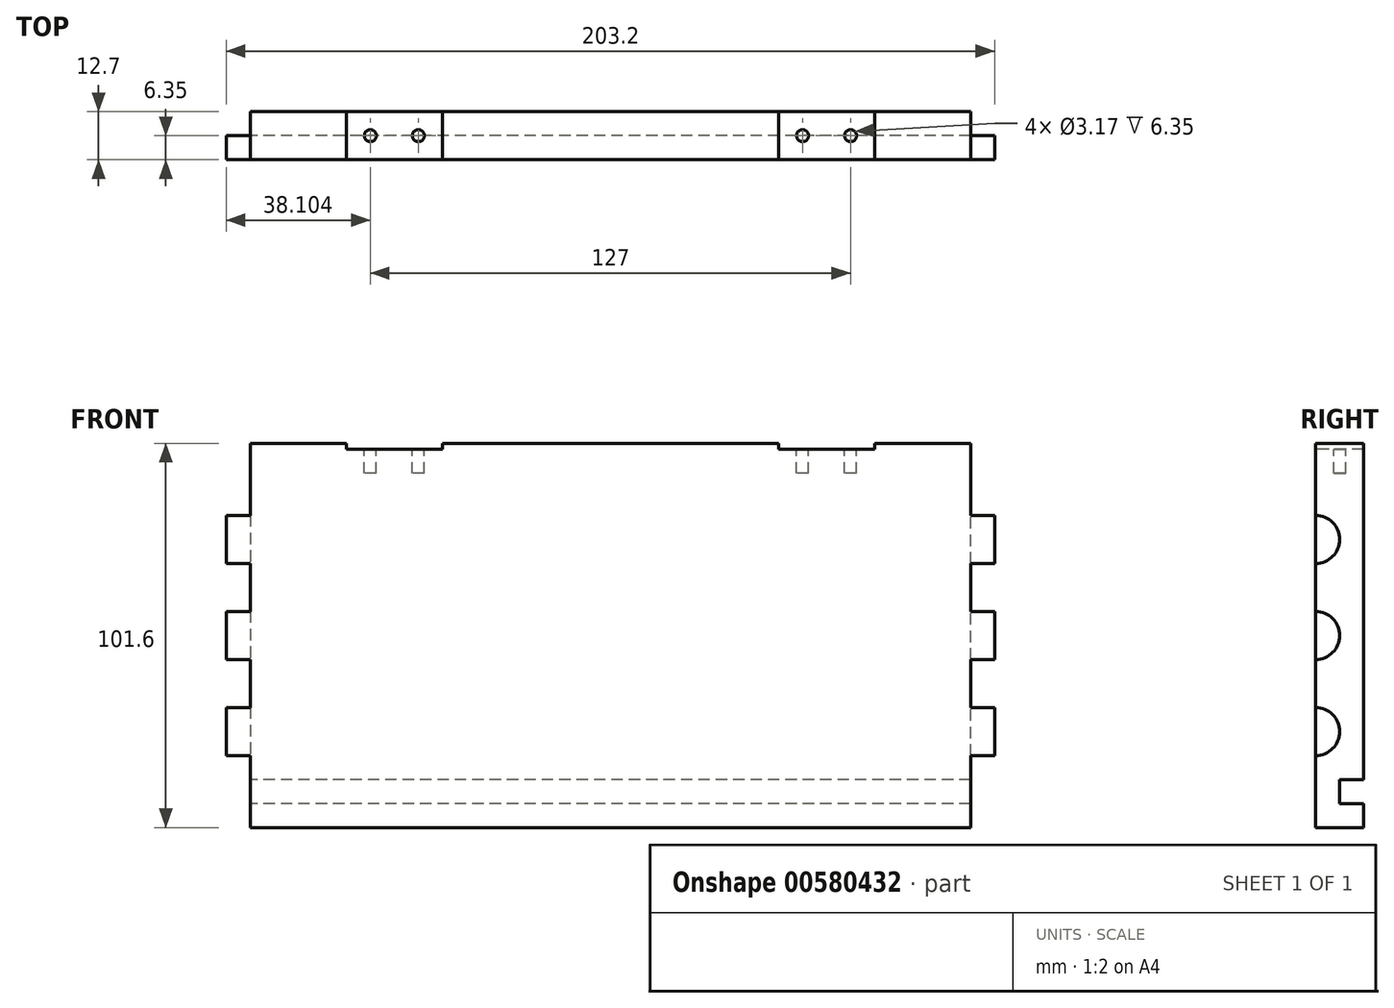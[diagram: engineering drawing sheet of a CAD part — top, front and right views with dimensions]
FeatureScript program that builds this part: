
annotation { "Feature Type Name" : "Feature", "Feature Type Description" : "" }
export const myFeature = defineFeature(function(context is Context, id is Id, definition is map)
    precondition{}
    {
        {
            var Q0;
            Q0=qCreatedBy(makeId("Front.planeOp"),FACE);
            var sketch = newSketch(context, id + "F0", { "sketchPlane" : qUnion([Q0])});
            skLineSegment(sketch, "E0.bottom", {"start": v(104.93, 50.8) * mm, "end": v(-98.27, 50.8) * mm});
            skLineSegment(sketch, "E0.top", {"start": v(104.93, -50.8) * mm, "end": v(-98.27, -50.8) * mm});
            skLineSegment(sketch, "E0.left", {"start": v(104.93, 50.8) * mm, "end": v(104.93, -50.8) * mm});
            skLineSegment(sketch, "E0.right", {"start": v(-98.27, 50.8) * mm, "end": v(-98.27, -50.8) * mm});
            skPoint(sketch, "E0.middle", {"position": v(3.33, 0) * mm});
            skSolve(sketch);
        }
        {
            var Q0;
            Q0=makeQuery(id+"F0.imprint","IMPRINT",FACE,{"disambiguationData":[TD([[makeQuery(id+"F0.imprint","IMPRINT",EDGE,{"derivedFrom":sQuery(id+"F0.wireOp",EDGE,"E0.bottom")}),1.0]])]});
            extrude(context, id + "F1", {"entities" : qUnion([Q0]), "depth" : 12.7 * mm, "offsetDistance" : 25.4 * mm});
        }
        {
            var Q0;
            Q0=makeQuery(id+"F1.opExtrude","CAP_FACE",FACE,{"disambiguationData":[OSD([sQuery(id+"F0.wireOp",EDGE,"E0.bottom"),sQuery(id+"F0.wireOp",EDGE,"E0.top"),sQuery(id+"F0.wireOp",EDGE,"E0.left"),sQuery(id+"F0.wireOp",EDGE,"E0.right")])],"isStart":true});
            var sketch = newSketch(context, id + "F2", { "sketchPlane" : qUnion([Q0])});
            skLineSegment(sketch, "E1.bottom", {"start": v(-104.93, -38.1) * mm, "end": v(98.27, -38.1) * mm});
            skLineSegment(sketch, "E1.top", {"start": v(-104.93, -44.45) * mm, "end": v(98.27, -44.45) * mm});
            skLineSegment(sketch, "E1.left", {"start": v(-104.93, -38.1) * mm, "end": v(-104.93, -44.45) * mm});
            skLineSegment(sketch, "E1.right", {"start": v(98.27, -38.1) * mm, "end": v(98.27, -44.45) * mm});
            skSolve(sketch);
        }
        {
            var Q0;
            Q0=makeQuery(id+"F2.imprint","IMPRINT",FACE,{"disambiguationData":[TD([[makeQuery(id+"F2.imprint","IMPRINT",EDGE,{"derivedFrom":sQuery(id+"F2.wireOp",EDGE,"E1.bottom")}),-1.0]])]});
            extrude(context, id + "F3", {"entities" : qUnion([Q0]), "operationType" : NewBodyOperationType.REMOVE, "oppositeDirection" : true, "depth" : 6.35 * mm, "offsetDistance" : 25.4 * mm});
        }
        {
            var Q0;
            Q0=makeQuery(id+"F1.opExtrude","SWEPT_FACE",FACE,{"disambiguationData":[OSD([sQuery(id+"F0.wireOp",EDGE,"E0.right")])]});
            var sketch = newSketch(context, id + "F4", { "sketchPlane" : qUnion([Q0])});
            skArc(sketch, "E2", {"start": v(12.7, 31.75) * mm, "mid": v(6.35, 25.4) * mm, "end": v(12.7, 19.05) * mm});
            skArc(sketch, "E3", {"start": v(12.7, 6.35) * mm, "mid": v(6.35, 0) * mm, "end": v(12.7, -6.35) * mm});
            skArc(sketch, "E4", {"start": v(12.7, -19.05) * mm, "mid": v(6.35, -25.4) * mm, "end": v(12.7, -31.75) * mm});
            skSolve(sketch);
        }
        {
            var Q0;
            Q0 = qSketchRegion(id + "F4", true);
            var Q1;
            {var subQ10=sQuery(id+"F4.wireOp",EDGE,"E2");Q1=makeQuery(id+"F4.imprint","IMPRINT",FACE,{"disambiguationData":[TD([[makeQuery(id+"F4.imprint","IMPRINT",EDGE,{"derivedFrom":subQ10}),-1.0]])]});}
            extrude(context, id + "F5", {"entities" : qUnion([Q0, Q1]), "operationType" : NewBodyOperationType.REMOVE, "oppositeDirection" : true, "depth" : 6.35 * mm, "offsetDistance" : 25.4 * mm});
        }
        {
            var Q0;
            Q0=makeQuery(id+"F1.opExtrude","SWEPT_FACE",FACE,{"disambiguationData":[OSD([sQuery(id+"F0.wireOp",EDGE,"E0.left")])]});
            var sketch = newSketch(context, id + "F6", { "sketchPlane" : qUnion([Q0])});
            skArc(sketch, "E5", {"start": v(-12.7, 19.05) * mm, "mid": v(-6.35, 25.4) * mm, "end": v(-12.7, 31.75) * mm});
            skArc(sketch, "E6", {"start": v(-12.7, -6.35) * mm, "mid": v(-6.35, 0) * mm, "end": v(-12.7, 6.35) * mm});
            skArc(sketch, "E7", {"start": v(-12.7, -31.75) * mm, "mid": v(-6.35, -25.4) * mm, "end": v(-12.7, -19.05) * mm});
            skSolve(sketch);
        }
        {
            var Q0;
            Q0 = qSketchRegion(id + "F6", true);
            var Q1;
            {var subQ10=sQuery(id+"F6.wireOp",EDGE,"E5");Q1=makeQuery(id+"F6.imprint","IMPRINT",FACE,{"disambiguationData":[TD([[makeQuery(id+"F6.imprint","IMPRINT",EDGE,{"derivedFrom":subQ10}),-1.0]])]});}
            extrude(context, id + "F7", {"entities" : qUnion([Q0, Q1]), "operationType" : NewBodyOperationType.REMOVE, "oppositeDirection" : true, "depth" : 6.35 * mm, "offsetDistance" : 25.4 * mm});
        }
        {
            var Q0;
            Q0=makeQuery(id+"F1.opExtrude","SWEPT_FACE",FACE,{"disambiguationData":[OSD([sQuery(id+"F0.wireOp",EDGE,"E0.bottom")])]});
            var sketch = newSketch(context, id + "F8", { "sketchPlane" : qUnion([Q0])});
            skLineSegment(sketch, "E8.bottom", {"start": v(-66.52, 0) * mm, "end": v(-41.12, 0) * mm});
            skLineSegment(sketch, "E8.top", {"start": v(-66.52, -12.7) * mm, "end": v(-41.12, -12.7) * mm});
            skLineSegment(sketch, "E8.left", {"start": v(-66.52, 0) * mm, "end": v(-66.52, -12.7) * mm});
            skLineSegment(sketch, "E8.right", {"start": v(-41.12, 0) * mm, "end": v(-41.12, -12.7) * mm});
            skLineSegment(sketch, "E9.bottom", {"start": v(47.78, 0) * mm, "end": v(73.18, 0) * mm});
            skLineSegment(sketch, "E9.top", {"start": v(47.78, -12.7) * mm, "end": v(73.18, -12.7) * mm});
            skLineSegment(sketch, "E9.left", {"start": v(47.78, 0) * mm, "end": v(47.78, -12.7) * mm});
            skLineSegment(sketch, "E9.right", {"start": v(73.18, 0) * mm, "end": v(73.18, -12.7) * mm});
            skSolve(sketch);
        }
        {
            var Q0;
            Q0 = qSketchRegion(id + "F8", true);
            extrude(context, id + "F9", {"entities" : qUnion([Q0]), "operationType" : NewBodyOperationType.REMOVE, "oppositeDirection" : true, "depth" : 1.59 * mm, "offsetDistance" : 25.4 * mm});
        }
        {
            var Q0;
            Q0=makeQuery(id+"F9.boolean.opBoolean","COPY",FACE,{"derivedFrom":makeQuery(id+"F9.opExtrude","CAP_FACE",FACE,{"disambiguationData":[OSD([sQuery(id+"F8.wireOp",EDGE,"E8.bottom"),sQuery(id+"F8.wireOp",EDGE,"E8.top"),sQuery(id+"F8.wireOp",EDGE,"E8.left"),sQuery(id+"F8.wireOp",EDGE,"E8.right")])],"isStart":false})});
            var sketch = newSketch(context, id + "F10", { "sketchPlane" : qUnion([Q0])});
            skCircle(sketch, "E10", {"center": v(-60.17, -6.35) * mm, "radius": 1.59 * mm});
            skCircle(sketch, "E11", {"center": v(-47.47, -6.35) * mm, "radius": 1.59 * mm});
            skSolve(sketch);
        }
        {
            var Q0;
            Q0 = qSketchRegion(id + "F10", true);
            extrude(context, id + "F11", {"entities" : qUnion([Q0]), "operationType" : NewBodyOperationType.REMOVE, "oppositeDirection" : true, "depth" : 6.35 * mm, "offsetDistance" : 25.4 * mm});
        }
        {
            var Q0;
            Q0=makeQuery(id+"F9.boolean.opBoolean","COPY",FACE,{"derivedFrom":makeQuery(id+"F9.opExtrude","CAP_FACE",FACE,{"disambiguationData":[OSD([sQuery(id+"F8.wireOp",EDGE,"E9.bottom"),sQuery(id+"F8.wireOp",EDGE,"E9.top"),sQuery(id+"F8.wireOp",EDGE,"E9.left"),sQuery(id+"F8.wireOp",EDGE,"E9.right")])],"isStart":false})});
            var sketch = newSketch(context, id + "F12", { "sketchPlane" : qUnion([Q0])});
            skCircle(sketch, "E12", {"center": v(54.13, -6.35) * mm, "radius": 1.59 * mm});
            skCircle(sketch, "E13", {"center": v(66.83, -6.35) * mm, "radius": 1.59 * mm});
            skSolve(sketch);
        }
        {
            var Q0;
            Q0 = qSketchRegion(id + "F12", true);
            extrude(context, id + "F13", {"entities" : qUnion([Q0]), "operationType" : NewBodyOperationType.REMOVE, "oppositeDirection" : true, "depth" : 6.35 * mm, "offsetDistance" : 25.4 * mm});
        }
    });
